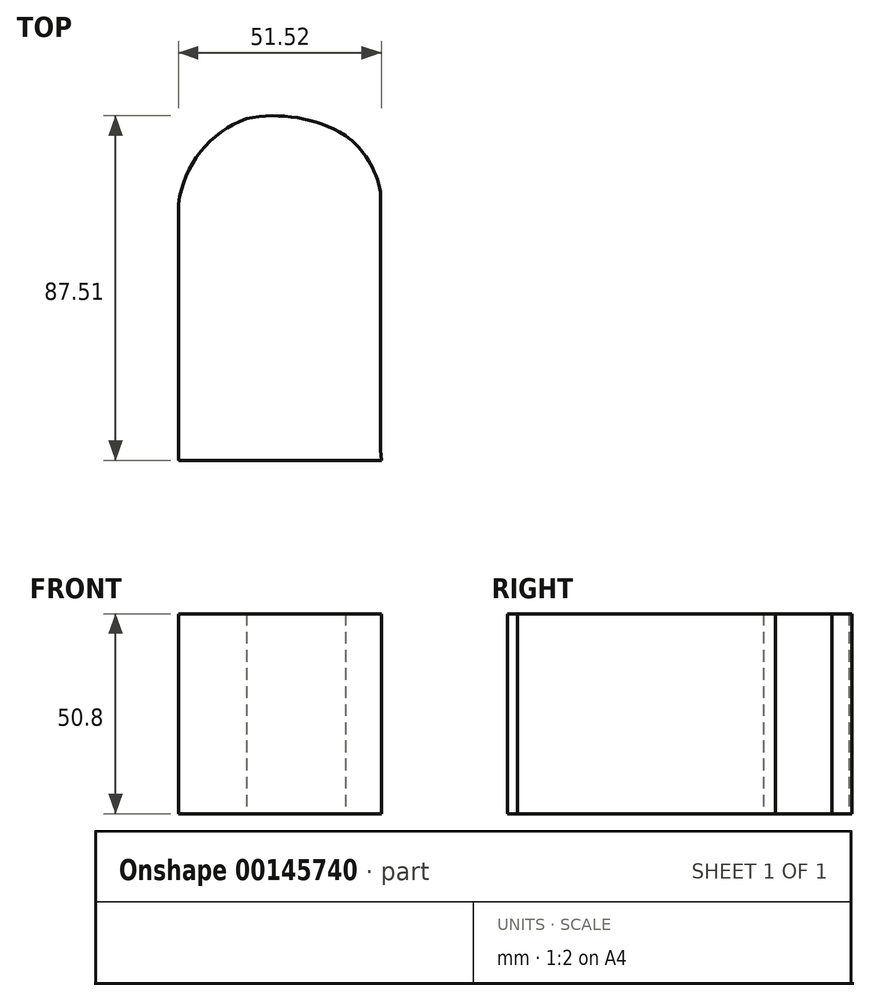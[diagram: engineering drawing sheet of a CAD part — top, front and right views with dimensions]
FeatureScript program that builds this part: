
annotation { "Feature Type Name" : "Feature", "Feature Type Description" : "" }
export const myFeature = defineFeature(function(context is Context, id is Id, definition is map)
    precondition{}
    {
        {
            var Q0;
            Q0=qCreatedBy(makeId("Top.planeOp"),FACE);
            var sketch = newSketch(context, id + "F0", { "sketchPlane" : qUnion([Q0])});
            skArc(sketch, "E0", {"start": v(-21.5, 45.73) * mm, "mid": v(-33.16, 37.3) * mm, "end": v(-38.74, 24.03) * mm});
            skArc(sketch, "E1", {"start": v(3.65, 41.48) * mm, "mid": v(-8.53, 45.94) * mm, "end": v(-21.5, 45.73) * mm});
            skArc(sketch, "E2", {"start": v(12.57, 27.08) * mm, "mid": v(9.49, 35.13) * mm, "end": v(3.65, 41.48) * mm});
            skLineSegment(sketch, "E3", {"start": v(-38.74, 24.03) * mm, "end": v(-38.74, -10.44) * mm});
            skLineSegment(sketch, "E4", {"start": v(12.57, 27.08) * mm, "end": v(12.57, -13.9) * mm});
            skLineSegment(sketch, "E5", {"start": v(-38.74, -10.44) * mm, "end": v(-38.74, -14.1) * mm});
            skLineSegment(sketch, "E6", {"start": v(-38.74, -14.1) * mm, "end": v(-38.74, -41.07) * mm});
            skLineSegment(sketch, "E7", {"start": v(12.57, -13.9) * mm, "end": v(12.57, -38.43) * mm});
            skLineSegment(sketch, "E8", {"start": v(-38.74, -41.07) * mm, "end": v(12.78, -41.07) * mm});
            skLineSegment(sketch, "E9", {"start": v(12.57, -38.43) * mm, "end": v(12.78, -41.07) * mm});
            skSolve(sketch);
        }
        {
            var Q0;
            Q0 = qSketchRegion(id + "F0", true);
            extrude(context, id + "F1", {"entities" : qUnion([Q0]), "depth" : 50.8 * mm});
        }
        {
            var Q0;
            Q0 = qSketchRegion(id + "F0", true);
            extrude(context, id + "F2", {"entities" : qUnion([Q0]), "operationType" : NewBodyOperationType.ADD, "depth" : 25.4 * mm});
        }
    });
